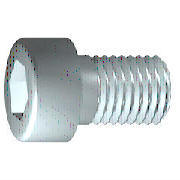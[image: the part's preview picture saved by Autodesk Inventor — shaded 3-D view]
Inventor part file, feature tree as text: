
AUTODESK INVENTOR PART (.ipt)
format: ipt  version: 2018 (Build 220112000, 112)  size: 186,880 bytes
history: native  units: mm (DEFAULTED — no unit token found)
features: sketch x2, extrude x1, plane x1, fillet x1
ambient origin geometry x7: Origin, YZ Plane, XY Plane, X Axis, Y Axis, Z Axis, Center Point
bodies: Solid1 (feature_tree), Body (feature_tree)
feature tree (5):
  extrude  "Slot"  Depth=3.0mm
  plane  "Work Plane1"
  fillet  "Fillet2"  Radius=3.0mm
  sketch  "Sketch1"  dims[d1=19.08655mm d2=0.306825mm d3=3.0mm]
  sketch  "Sketch2"  dims[d4=1.5mm d5=60.0deg d6=3.0mm d7=3.0mm d8=2.886751mm d9=5.5mm d10=90.0deg d11=10.0mm d12=0.0mm d13=19.08655mm d14=0.0mm d15=0.306725mm d16=0.306725mm d17=0.3mm d19=0.0mm d26=20.0mm d27=45.0deg d28=0.0mm d29=0.0mm d30=0.1mm]
